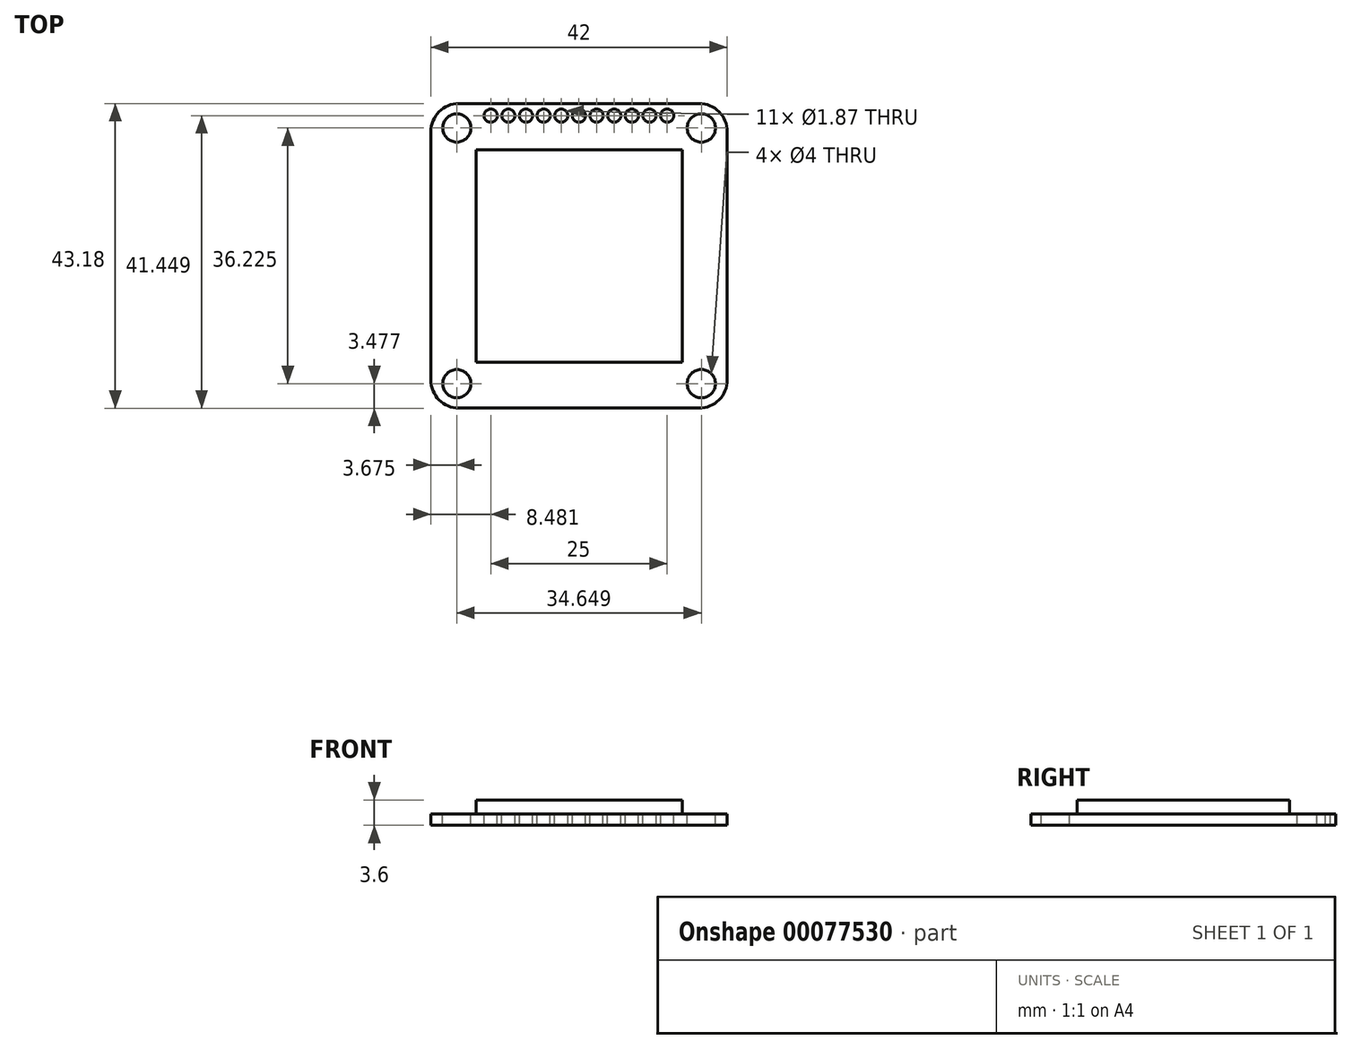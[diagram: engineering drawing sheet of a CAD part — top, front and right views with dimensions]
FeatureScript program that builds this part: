
annotation { "Feature Type Name" : "Feature", "Feature Type Description" : "" }
export const myFeature = defineFeature(function(context is Context, id is Id, definition is map)
    precondition{}
    {
        {
            var Q0;
            Q0=qCreatedBy(makeId("Top.planeOp"),FACE);
            var sketch = newSketch(context, id + "F0", { "sketchPlane" : qUnion([Q0])});
            skLineSegment(sketch, "E0.bottom", {"start": v(-17, 21.58) * mm, "end": v(17, 21.58) * mm});
            skLineSegment(sketch, "E0.top", {"start": v(-17, -21.59) * mm, "end": v(17, -21.59) * mm});
            skLineSegment(sketch, "E0.left", {"start": v(-21, 17.58) * mm, "end": v(-21, -17.59) * mm});
            skLineSegment(sketch, "E0.right", {"start": v(21, 17.58) * mm, "end": v(21, -17.59) * mm});
            skPoint(sketch, "E0.middle", {"position": v(0, 0) * mm});
            skLineSegment(sketch, "E1.bottom", {"start": v(-17.32, 18.11) * mm, "end": v(17.32, 18.11) * mm, "construction": true});
            skLineSegment(sketch, "E1.top", {"start": v(-17.32, -18.11) * mm, "end": v(17.32, -18.11) * mm, "construction": true});
            skLineSegment(sketch, "E1.left", {"start": v(-17.32, 18.11) * mm, "end": v(-17.32, -18.11) * mm, "construction": true});
            skLineSegment(sketch, "E1.right", {"start": v(17.32, 18.11) * mm, "end": v(17.32, -18.11) * mm, "construction": true});
            skCircle(sketch, "E2", {"center": v(-17.32, 18.11) * mm, "radius": 2 * mm});
            skCircle(sketch, "E3", {"center": v(17.32, 18.11) * mm, "radius": 2 * mm});
            skCircle(sketch, "E4", {"center": v(17.32, -18.11) * mm, "radius": 2 * mm});
            skCircle(sketch, "E5", {"center": v(-17.32, -18.11) * mm, "radius": 2 * mm});
            skCircle(sketch, "E6", {"center": v(-12.52, 19.86) * mm, "radius": 0.93 * mm});
            skCircle(sketch, "E7.1.0.0", {"center": v(-10.02, 19.86) * mm, "radius": 0.93 * mm});
            skCircle(sketch, "E7.2.0.0", {"center": v(-7.52, 19.86) * mm, "radius": 0.93 * mm});
            skCircle(sketch, "E7.3.0.0", {"center": v(-5.02, 19.86) * mm, "radius": 0.93 * mm});
            skCircle(sketch, "E7.4.0.0", {"center": v(-2.52, 19.86) * mm, "radius": 0.93 * mm});
            skCircle(sketch, "E7.5.0.0", {"center": v(-0.02, 19.86) * mm, "radius": 0.93 * mm});
            skCircle(sketch, "E7.6.0.0", {"center": v(2.48, 19.86) * mm, "radius": 0.93 * mm});
            skCircle(sketch, "E7.7.0.0", {"center": v(4.98, 19.86) * mm, "radius": 0.93 * mm});
            skCircle(sketch, "E7.8.0.0", {"center": v(7.48, 19.86) * mm, "radius": 0.93 * mm});
            skCircle(sketch, "E7.9.0.0", {"center": v(9.98, 19.86) * mm, "radius": 0.93 * mm});
            skCircle(sketch, "E7.10.0.0", {"center": v(12.48, 19.86) * mm, "radius": 0.93 * mm});
            skLineSegment(sketch, "E7.direction1", {"start": v(-12.52, 19.86) * mm, "end": v(-10.02, 19.86) * mm, "construction": true});
            skPoint(sketch, "E8.visualSharp", {"position": v(-21, 21.58) * mm});
            skArc(sketch, "E8.filletArc", {"start": v(-17, 21.58) * mm, "mid": v(-19.83, 20.41) * mm, "end": v(-21, 17.58) * mm});
            skPoint(sketch, "E9.visualSharp", {"position": v(21, 21.58) * mm});
            skArc(sketch, "E9.filletArc", {"start": v(21, 17.58) * mm, "mid": v(19.83, 20.41) * mm, "end": v(17, 21.58) * mm});
            skPoint(sketch, "E10.visualSharp", {"position": v(21, -21.59) * mm});
            skArc(sketch, "E10.filletArc", {"start": v(17, -21.59) * mm, "mid": v(19.83, -20.41) * mm, "end": v(21, -17.59) * mm});
            skPoint(sketch, "E11.visualSharp", {"position": v(-21, -21.59) * mm});
            skArc(sketch, "E11.filletArc", {"start": v(-21, -17.59) * mm, "mid": v(-19.83, -20.41) * mm, "end": v(-17, -21.59) * mm});
            skLineSegment(sketch, "E12.bottom", {"start": v(-14.61, 15.05) * mm, "end": v(14.61, 15.05) * mm});
            skLineSegment(sketch, "E12.top", {"start": v(-14.61, -15.05) * mm, "end": v(14.61, -15.05) * mm});
            skLineSegment(sketch, "E12.left", {"start": v(-14.61, 15.05) * mm, "end": v(-14.61, -15.05) * mm});
            skLineSegment(sketch, "E12.right", {"start": v(14.61, 15.05) * mm, "end": v(14.61, -15.05) * mm});
            skSolve(sketch);
        }
        {
            var Q0;
            Q0=makeQuery(id+"F0.imprint","IMPRINT",FACE,{"disambiguationData":[TD([[makeQuery(id+"F0.imprint","IMPRINT",EDGE,{"derivedFrom":sQuery(id+"F0.wireOp",EDGE,"E0.bottom")}),-1.0]])]});
            var Q1;
            Q1=makeQuery(id+"F0.imprint","IMPRINT",FACE,{"disambiguationData":[TD([[makeQuery(id+"F0.imprint","IMPRINT",EDGE,{"derivedFrom":sQuery(id+"F0.wireOp",EDGE,"E12.bottom")}),-1.0]])]});
            extrude(context, id + "F1", {"entities" : qUnion([Q0, Q1]), "oppositeDirection" : true, "depth" : 1.6 * mm});
        }
        {
            var Q0;
            Q0=makeQuery(id+"F0.imprint","IMPRINT",FACE,{"disambiguationData":[TD([[makeQuery(id+"F0.imprint","IMPRINT",EDGE,{"derivedFrom":sQuery(id+"F0.wireOp",EDGE,"E12.bottom")}),-1.0]])]});
            extrude(context, id + "F2", {"entities" : qUnion([Q0]), "operationType" : NewBodyOperationType.ADD, "depth" : 2 * mm});
        }
    });
